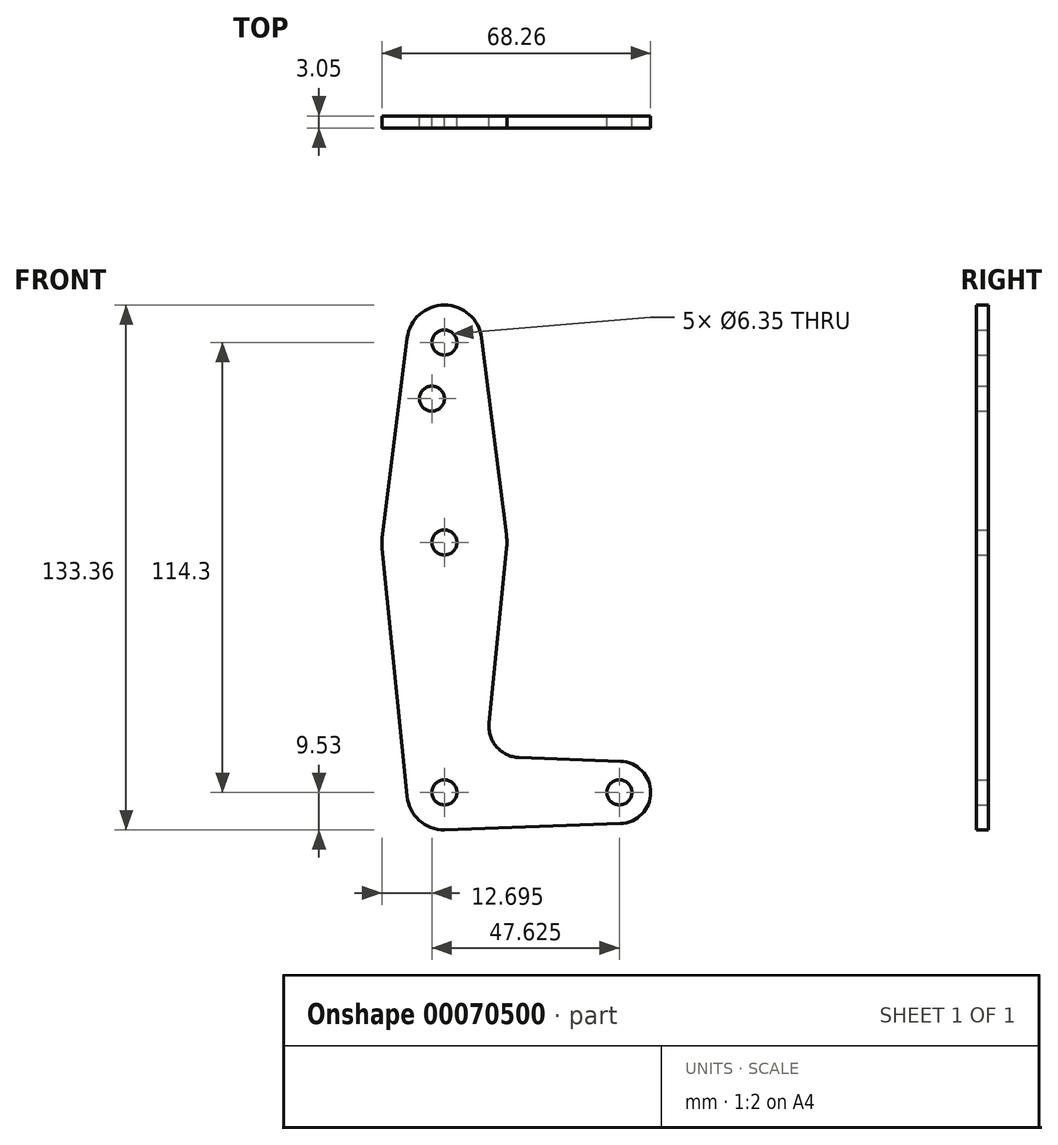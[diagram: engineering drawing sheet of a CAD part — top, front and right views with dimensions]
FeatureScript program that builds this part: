
annotation { "Feature Type Name" : "Feature", "Feature Type Description" : "" }
export const myFeature = defineFeature(function(context is Context, id is Id, definition is map)
    precondition{}
    {
        {
            var Q0;
            Q0=qCreatedBy(makeId("Front.planeOp"),FACE);
            var sketch = newSketch(context, id + "F0", { "sketchPlane" : qUnion([Q0])});
            skCircle(sketch, "E0", {"center": v(0, 0) * mm, "radius": 9.53 * mm});
            skCircle(sketch, "E1", {"center": v(0, 63.5) * mm, "radius": 15.88 * mm});
            skCircle(sketch, "E2", {"center": v(0, 114.3) * mm, "radius": 9.53 * mm});
            skCircle(sketch, "E3", {"center": v(44.45, 0) * mm, "radius": 7.94 * mm});
            skLineSegment(sketch, "E4", {"start": v(0, 114.3) * mm, "end": v(0, 0) * mm, "construction": true});
            skLineSegment(sketch, "E5", {"start": v(44.45, 0) * mm, "end": v(0, 0) * mm, "construction": true});
            skLineSegment(sketch, "E6", {"start": v(-15.75, 65.48) * mm, "end": v(-9.45, 115.5) * mm});
            skLineSegment(sketch, "E7", {"start": v(15.75, 65.48) * mm, "end": v(9.45, 115.5) * mm});
            skLineSegment(sketch, "E8", {"start": v(15.8, 61.91) * mm, "end": v(11.34, 17.6) * mm});
            skLineSegment(sketch, "E9", {"start": v(0, -9.53) * mm, "end": v(44.73, -7.93) * mm});
            skCircle(sketch, "E10", {"center": v(-3.17, 100.03) * mm, "radius": 3.18 * mm});
            skCircle(sketch, "E11", {"center": v(0, 63.5) * mm, "radius": 3.18 * mm});
            skCircle(sketch, "E12", {"center": v(0, 0) * mm, "radius": 3.18 * mm});
            skCircle(sketch, "E13", {"center": v(44.45, 0) * mm, "radius": 3.18 * mm});
            skCircle(sketch, "E14", {"center": v(0, 114.3) * mm, "radius": 3.18 * mm});
            skLineSegment(sketch, "E15", {"start": v(18.97, 8.85) * mm, "end": v(44.73, 7.93) * mm});
            skArc(sketch, "E16.filletArc", {"start": v(11.34, 17.6) * mm, "mid": v(13.26, 11.57) * mm, "end": v(18.97, 8.85) * mm});
            skLineSegment(sketch, "E17", {"start": v(-15.8, 61.91) * mm, "end": v(-9.48, -0.95) * mm});
            skSolve(sketch);
        }
        {
            var Q0;
            {var subQ1=sQuery(id+"F0.wireOp",EDGE,"E6");Q0=makeQuery(id+"F0.imprint","IMPRINT",FACE,{"disambiguationData":[TD([[makeQuery(id+"F0.imprint","IMPRINT",EDGE,{"derivedFrom":subQ1}),-1.0]])]});}
            var Q1;
            {var subQ0=sQuery(id+"F0.wireOp",EDGE,"E8");Q1=makeQuery(id+"F0.imprint","IMPRINT",FACE,{"disambiguationData":[TD([[makeQuery(id+"F0.imprint","IMPRINT",EDGE,{"derivedFrom":subQ0}),-1.0]])]});}
            var Q2;
            Q2=makeQuery(id+"F0.imprint","IMPRINT",FACE,{"disambiguationData":[TD([[makeQuery(id+"F0.imprint","IMPRINT",EDGE,{"derivedFrom":sQuery(id+"F0.wireOp",EDGE,"E11")}),-1.0]])]});
            var Q3;
            Q3=makeQuery(id+"F0.imprint","IMPRINT",FACE,{"disambiguationData":[TD([[makeQuery(id+"F0.imprint","IMPRINT",EDGE,{"derivedFrom":sQuery(id+"F0.wireOp",EDGE,"E12")}),-1.0]])]});
            var Q4;
            Q4=makeQuery(id+"F0.imprint","IMPRINT",FACE,{"disambiguationData":[TD([[makeQuery(id+"F0.imprint","IMPRINT",EDGE,{"derivedFrom":sQuery(id+"F0.wireOp",EDGE,"E13")}),-1.0]])]});
            var Q5;
            Q5=makeQuery(id+"F0.imprint","IMPRINT",FACE,{"disambiguationData":[TD([[makeQuery(id+"F0.imprint","IMPRINT",EDGE,{"derivedFrom":sQuery(id+"F0.wireOp",EDGE,"E14")}),-1.0]])]});
            extrude(context, id + "F1", {"entities" : qUnion([Q0, Q1, Q2, Q3, Q4, Q5]), "depth" : 3.05 * mm});
        }
    });
